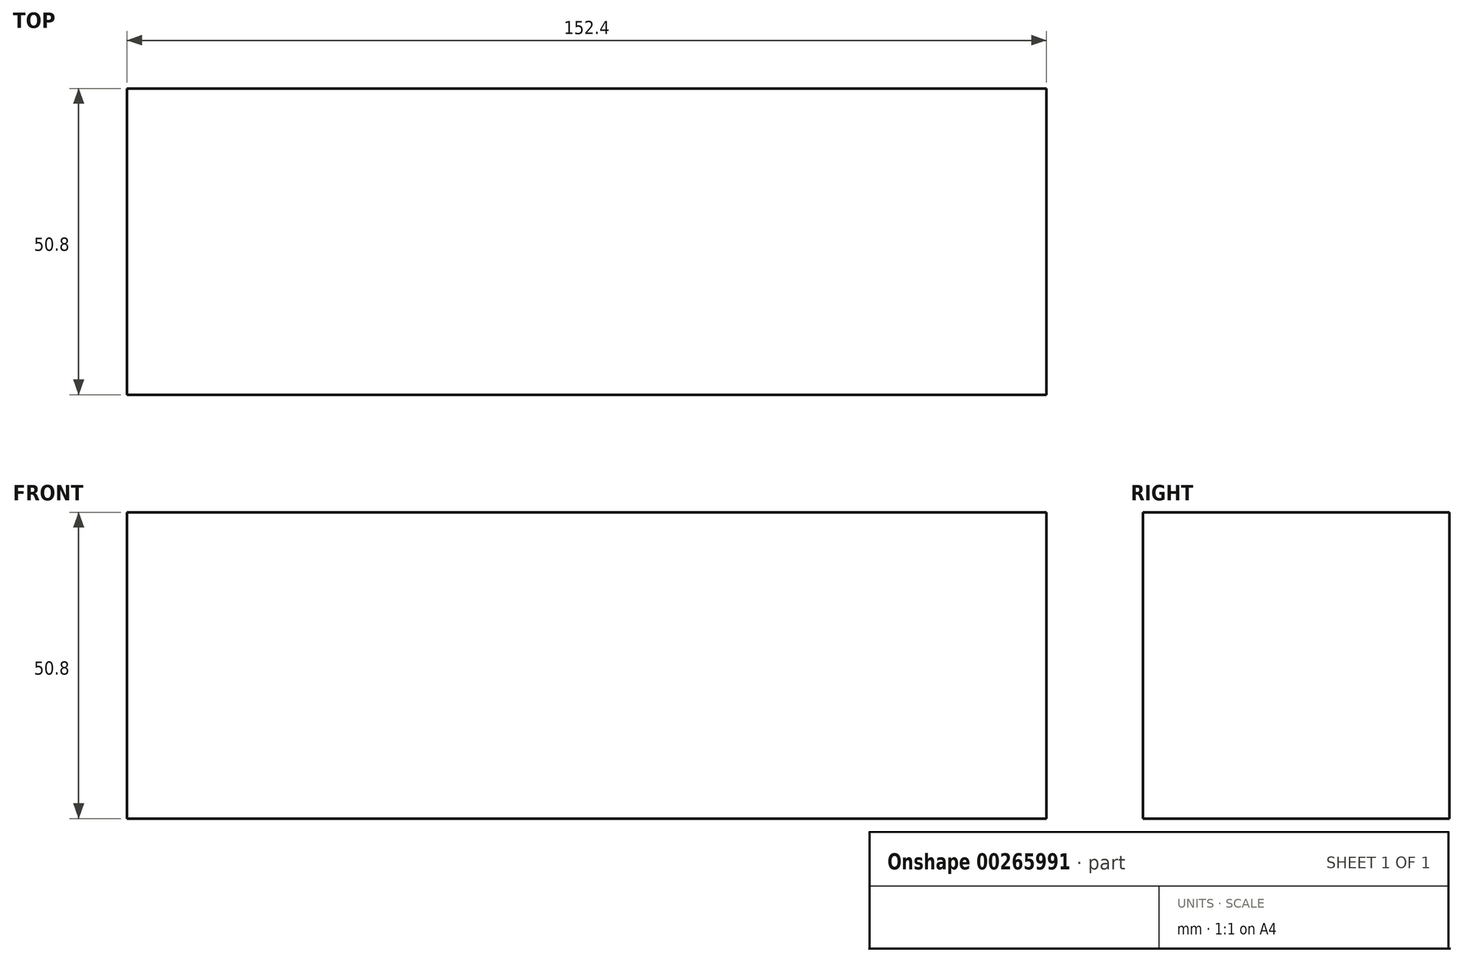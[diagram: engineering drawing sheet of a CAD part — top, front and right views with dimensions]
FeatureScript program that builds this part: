
annotation { "Feature Type Name" : "Feature", "Feature Type Description" : "" }
export const myFeature = defineFeature(function(context is Context, id is Id, definition is map)
    precondition{}
    {
        {
            var Q0;
            Q0=qCreatedBy(makeId("Top.planeOp"),FACE);
            var sketch = newSketch(context, id + "F0", { "sketchPlane" : qUnion([Q0])});
            skLineSegment(sketch, "E0.bottom", {"start": v(-113.3, 50.8) * mm, "end": v(39.1, 50.8) * mm});
            skLineSegment(sketch, "E0.top", {"start": v(-113.3, 0) * mm, "end": v(39.1, 0) * mm});
            skLineSegment(sketch, "E0.left", {"start": v(-113.3, 50.8) * mm, "end": v(-113.3, 0) * mm});
            skLineSegment(sketch, "E0.right", {"start": v(39.1, 50.8) * mm, "end": v(39.1, 0) * mm});
            skSolve(sketch);
        }
        {
            var Q0;
            Q0 = qSketchRegion(id + "F0", true);
            extrude(context, id + "F1", {"entities" : qUnion([Q0]), "depth" : 50.8 * mm});
        }
    });
